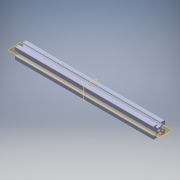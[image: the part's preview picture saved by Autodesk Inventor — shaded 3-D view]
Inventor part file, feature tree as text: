
AUTODESK INVENTOR PART (.ipt)
format: ipt  version: 2018 (Build 220112000, 112)  size: 376,320 bytes
history: native  units: in
note: dims shown in document units (in); Inventor stores cm internally (conversion verified against a paired STEP export)
features: extrude x1, plane x1, sketch x1, projected_geometry x1, fillet x1
ambient origin geometry x8: Origin, YZ Plane, XZ Plane, XY Plane, X Axis, Y Axis, Z Axis, Center Point
bodies: Solid1 (feature_tree)
feature tree (5):
  extrude  "Extrusion2"  [1 undecoded]
  plane  "Work Plane1"
  sketch  "Sketch3"  dims[d2=5.5118in d3=0.0in]
  projected_geometry  "Projected Loop2"
  fillet  "Fillet5"  [1 undecoded]
note: 2 required parameter values undecoded (feature->parameter linkage not recoverable at this tier; creation-order binding heuristic only, values carry confidence <= 0.55)
